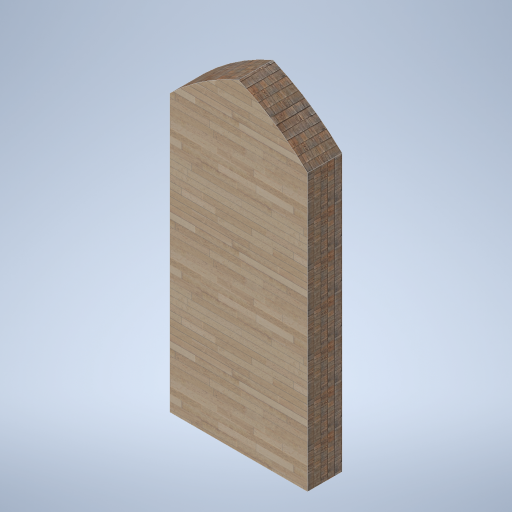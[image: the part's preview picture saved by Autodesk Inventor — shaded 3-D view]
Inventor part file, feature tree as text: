
AUTODESK INVENTOR PART (.ipt)
format: ipt  version: 2024.2 (Build 282272000, 272)  size: 416,768 bytes
history: native  units: in
note: dims shown in document units (in); Inventor stores cm internally (conversion verified against a paired STEP export)
features: sketch x7, other x3
ambient origin geometry x8: Origin, YZ Plane, XZ Plane, XY Plane, X Axis, Y Axis, Z Axis, Center Point
bodies: Solid1 (feature_tree)
feature tree (10):
  other  "door.ipt"
  other  "Solid1::door.ipt"
  other  "TaggingFeature1"
  sketch  "Sketch1"  dims[d0=0.3937in]
  sketch  "Sketch2"
  sketch  "草圖3"
  sketch  "草圖4"
  sketch  "草圖5"
  sketch  "草圖6"
  sketch  "草圖7"
